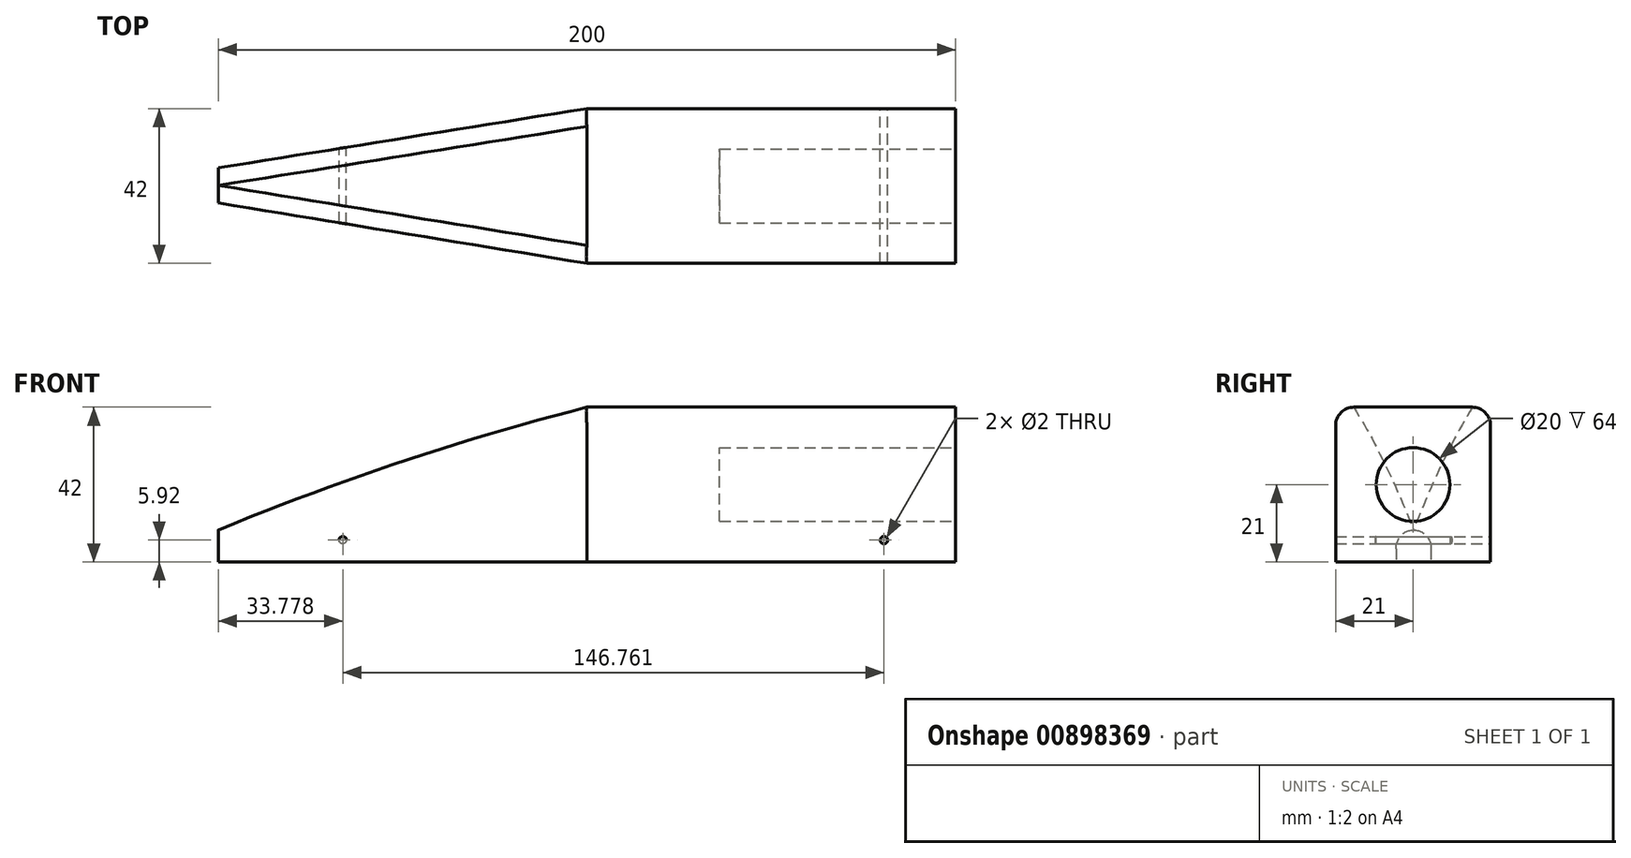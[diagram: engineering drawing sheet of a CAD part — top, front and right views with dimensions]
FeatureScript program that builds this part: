
annotation { "Feature Type Name" : "Feature", "Feature Type Description" : "" }
export const myFeature = defineFeature(function(context is Context, id is Id, definition is map)
    precondition{}
    {
        {
            var Q0;
            Q0=qCreatedBy(makeId("Top.planeOp"),FACE);
            var sketch = newSketch(context, id + "F0", { "sketchPlane" : qUnion([Q0])});
            skLineSegment(sketch, "E0.bottom", {"start": v(100, -21) * mm, "end": v(-100, -21) * mm});
            skLineSegment(sketch, "E0.top", {"start": v(100, 21) * mm, "end": v(-100, 21) * mm});
            skLineSegment(sketch, "E0.left", {"start": v(100, -21) * mm, "end": v(100, 21) * mm});
            skLineSegment(sketch, "E0.right", {"start": v(-100, -21) * mm, "end": v(-100, 21) * mm});
            skPoint(sketch, "E0.middle", {"position": v(0, 0) * mm});
            skSolve(sketch);
        }
        {
            var Q0;
            Q0 = qSketchRegion(id + "F0", true);
            extrude(context, id + "F1", {"entities" : qUnion([Q0]), "depth" : 42 * mm, "offsetDistance" : 25 * mm});
        }
        {
            var Q0;
            Q0=makeQuery(id+"F1.opExtrude","SWEPT_FACE",FACE,{"disambiguationData":[OSD([sQuery(id+"F0.wireOp",EDGE,"E0.left")])]});
            var sketch = newSketch(context, id + "F2", { "sketchPlane" : qUnion([Q0])});
            skCircle(sketch, "E1", {"center": v(0, 21) * mm, "radius": 10 * mm});
            skPoint(sketch, "E1.centerSnap0", {"position": v(-21, 21) * mm});
            skPoint(sketch, "E1.centerSnap1", {"position": v(0, 42) * mm});
            skSolve(sketch);
        }
        {
            var Q0;
            Q0 = qSketchRegion(id + "F2", true);
            extrude(context, id + "F3", {"entities" : qUnion([Q0]), "operationType" : NewBodyOperationType.REMOVE, "oppositeDirection" : true, "depth" : 64 * mm, "offsetDistance" : 25 * mm});
        }
        {
            var Q0;
            Q0=makeQuery(id+"F1.opExtrude","SWEPT_FACE",FACE,{"disambiguationData":[OSD([sQuery(id+"F0.wireOp",EDGE,"E0.top")])]});
            var sketch = newSketch(context, id + "F4", { "sketchPlane" : qUnion([Q0])});
            skCircle(sketch, "E2", {"center": v(-80.54, 5.92) * mm, "radius": 1 * mm});
            skCircle(sketch, "E3", {"center": v(66.22, 5.92) * mm, "radius": 1 * mm});
            skSolve(sketch);
        }
        {
            var Q0;
            Q0 = qSketchRegion(id + "F4", true);
            extrude(context, id + "F5", {"entities" : qUnion([Q0]), "operationType" : NewBodyOperationType.REMOVE, "oppositeDirection" : true, "depth" : 92.1 * mm, "offsetDistance" : 25 * mm});
        }
        {
            var Q0;
            Q0=makeQuery(id+"F1.opExtrude","SWEPT_FACE",FACE,{"disambiguationData":[OSD([sQuery(id+"F0.wireOp",EDGE,"E0.bottom")])]});
            var sketch = newSketch(context, id + "F6", { "sketchPlane" : qUnion([Q0])});
            skArc(sketch, "E4", {"start": v(0, 42) * mm, "mid": v(-50.59, 27.1) * mm, "end": v(-100, 8.67) * mm});
            skSolve(sketch);
        }
        {
            var Q0;
            Q0 = qSketchRegion(id + "F6", true);
            var Q1;
            {var subQ0=sQuery(id+"F6.wireOp",EDGE,"E4");Q1=makeQuery(id+"F6.imprint","IMPRINT",FACE,{"disambiguationData":[TD([[makeQuery(id+"F6.imprint","IMPRINT",EDGE,{"derivedFrom":subQ0}),-1.0]])]});}
            extrude(context, id + "F7", {"entities" : qUnion([Q0, Q1]), "operationType" : NewBodyOperationType.REMOVE, "oppositeDirection" : true, "depth" : 50.1 * mm, "offsetDistance" : 25 * mm});
        }
        {
            var Q0;
            Q0=makeQuery(id+"F1.opExtrude","CAP_FACE",FACE,{"disambiguationData":[OSD([sQuery(id+"F0.wireOp",EDGE,"E0.bottom"),sQuery(id+"F0.wireOp",EDGE,"E0.top"),sQuery(id+"F0.wireOp",EDGE,"E0.left"),sQuery(id+"F0.wireOp",EDGE,"E0.right")])],"isStart":true});
            var sketch = newSketch(context, id + "F8", { "sketchPlane" : qUnion([Q0])});
            skLineSegment(sketch, "E5", {"start": v(-100, -4.88) * mm, "end": v(0, -21) * mm});
            skLineSegment(sketch, "E6", {"start": v(-100, 4.6) * mm, "end": v(0, 21) * mm});
            skSolve(sketch);
        }
        {
            var Q0;
            Q0 = qSketchRegion(id + "F8", true);
            var Q1;
            {var subQ0=sQuery(id+"F8.wireOp",EDGE,"E5");Q1=makeQuery(id+"F8.imprint","IMPRINT",FACE,{"disambiguationData":[TD([[makeQuery(id+"F8.imprint","IMPRINT",EDGE,{"derivedFrom":subQ0}),-1.0]])]});}
            var Q2;
            {var subQ0=sQuery(id+"F8.wireOp",EDGE,"E6");Q2=makeQuery(id+"F8.imprint","IMPRINT",FACE,{"disambiguationData":[TD([[makeQuery(id+"F8.imprint","IMPRINT",EDGE,{"derivedFrom":subQ0}),1.0]])]});}
            extrude(context, id + "F9", {"entities" : qUnion([Q0, Q1, Q2]), "operationType" : NewBodyOperationType.REMOVE, "oppositeDirection" : true, "depth" : 75.3 * mm, "offsetDistance" : 25 * mm});
        }
        {
            var Q0;
            Q0=makeQuery(id+"F1.opExtrude","CAP_EDGE",EDGE,{"disambiguationData":[OSD([sQuery(id+"F0.wireOp",EDGE,"E0.top")])],"isStart":false});
            var Q1;
            Q1=makeQuery(id+"F1.opExtrude","CAP_EDGE",EDGE,{"disambiguationData":[OSD([sQuery(id+"F0.wireOp",EDGE,"E0.bottom")])],"isStart":false});
            var Q2;
            Q2=makeQuery(id+"F9.boolean.opBoolean","INTERSECT",EDGE,{"derivedFrom":[makeQuery(id+"F7.boolean.opBoolean","COPY",FACE,{"derivedFrom":makeQuery(id+"F7.opExtrude","SWEPT_FACE",FACE,{"disambiguationData":[OSD([sQuery(id+"F6.wireOp",EDGE,"E4")])]})}),makeQuery(id+"F9.opExtrude","SWEPT_FACE",FACE,{"disambiguationData":[OSD([sQuery(id+"F8.wireOp",EDGE,"E6")])]})]});
            var Q3;
            Q3=makeQuery(id+"F9.boolean.opBoolean","INTERSECT",EDGE,{"derivedFrom":[makeQuery(id+"F7.boolean.opBoolean","COPY",FACE,{"derivedFrom":makeQuery(id+"F7.opExtrude","SWEPT_FACE",FACE,{"disambiguationData":[OSD([sQuery(id+"F6.wireOp",EDGE,"E4")])]})}),makeQuery(id+"F9.opExtrude","SWEPT_FACE",FACE,{"disambiguationData":[OSD([sQuery(id+"F8.wireOp",EDGE,"E5")])]})]});
            var Q4;
            Q4=makeQuery(id+"F9.boolean.opBoolean","COPY",EDGE,{"derivedFrom":makeQuery(id+"F9.opExtrude","CAP_EDGE",EDGE,{"disambiguationData":[OSD([sQuery(id+"F8.wireOp",EDGE,"E5")])],"isStart":true})});
            var Q5;
            Q5=makeQuery(id+"F9.boolean.opBoolean","COPY",EDGE,{"derivedFrom":makeQuery(id+"F9.opExtrude","CAP_EDGE",EDGE,{"disambiguationData":[OSD([sQuery(id+"F8.wireOp",EDGE,"E6")])],"isStart":true})});
            fillet(context, id + "F10", {"entities" : qUnion([Q0, Q1, Q2, Q3, Q4, Q5]), "radius" : 5 * mm, "tangentPropagation" : true, "allowEdgeOverflow" : false});
        }
    });
